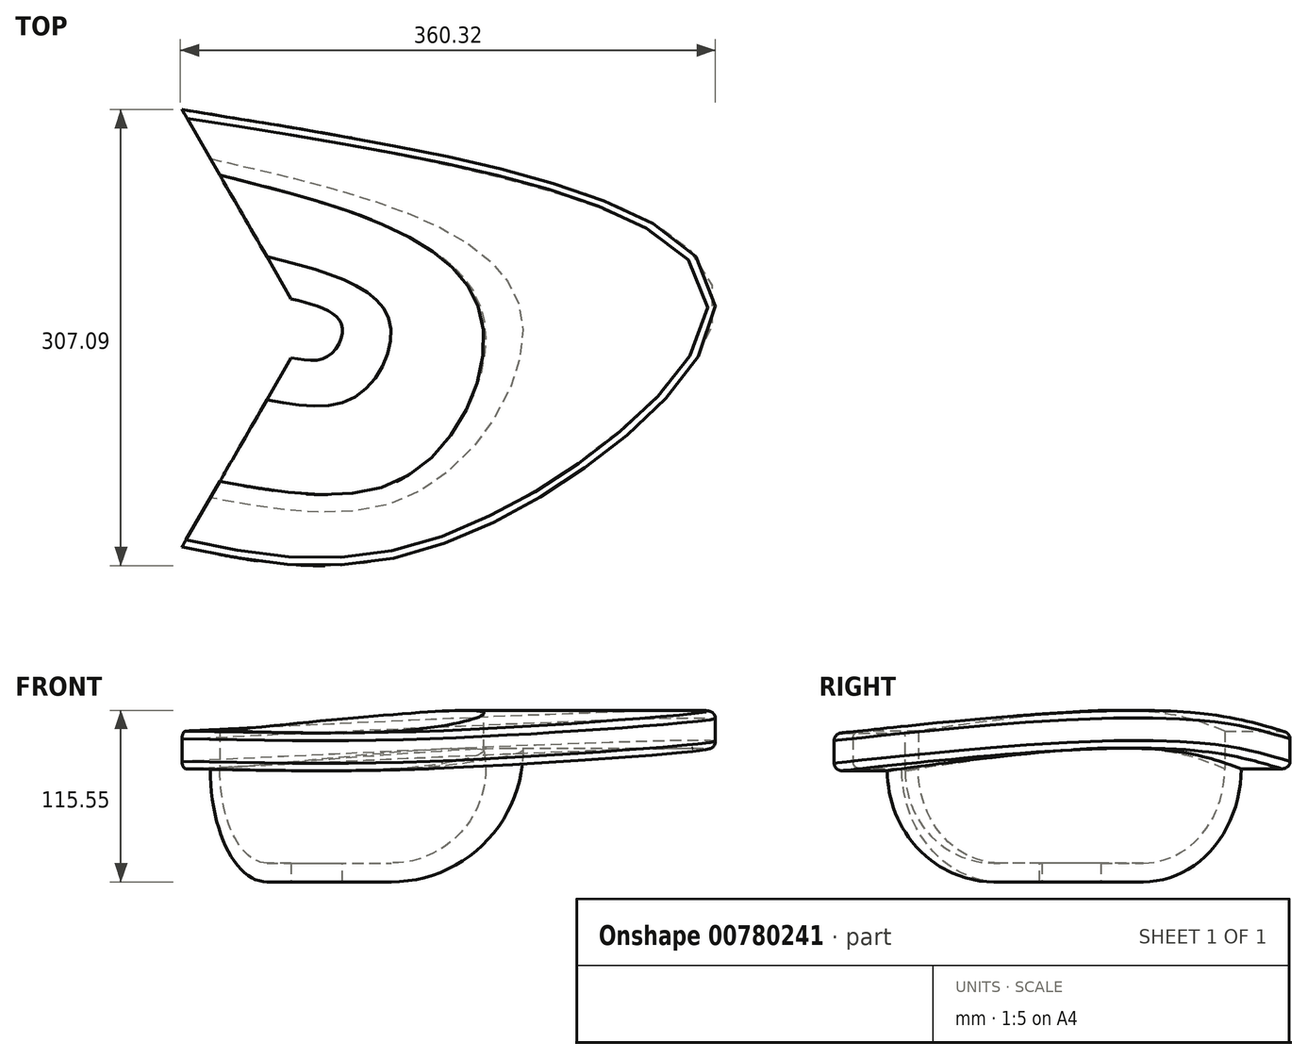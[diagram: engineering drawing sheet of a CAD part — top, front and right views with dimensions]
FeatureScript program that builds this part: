
annotation { "Feature Type Name" : "Feature", "Feature Type Description" : "" }
export const myFeature = defineFeature(function(context is Context, id is Id, definition is map)
    precondition{}
    {
        {
            var Q0;
            Q0=qCreatedBy(makeId("Front.planeOp"),FACE);
            var sketch = newSketch(context, id + "F0", { "sketchPlane" : qUnion([Q0])});
            skLineSegment(sketch, "E0.bottom", {"start": v(-53.34, -12.7) * mm, "end": v(-20.59, -12.7) * mm});
            skLineSegment(sketch, "E0.top", {"start": v(-53.34, -25.4) * mm, "end": v(-20.59, -25.4) * mm});
            skLineSegment(sketch, "E0.left", {"start": v(-53.34, -12.7) * mm, "end": v(-53.34, -25.4) * mm});
            skLineSegment(sketch, "E0.right", {"start": v(-20.59, -12.7) * mm, "end": v(-20.59, -25.4) * mm, "construction": true});
            skLineSegment(sketch, "E1.bottom", {"start": v(41.63, 88.9) * mm, "end": v(195.31, 88.9) * mm});
            skLineSegment(sketch, "E1.top", {"start": v(68.31, 63.5) * mm, "end": v(195.31, 63.5) * mm});
            skLineSegment(sketch, "E1.left", {"start": v(41.63, 88.9) * mm, "end": v(41.63, 63.5) * mm});
            skLineSegment(sketch, "E1.right", {"start": v(195.31, 88.9) * mm, "end": v(195.31, 63.5) * mm});
            skArc(sketch, "E2", {"start": v(-20.59, -25.4) * mm, "mid": v(42.28, 0.64) * mm, "end": v(68.31, 63.5) * mm});
            skArc(sketch, "E3", {"start": v(-20.59, -12.7) * mm, "mid": v(28.6, 10.64) * mm, "end": v(41.63, 63.5) * mm});
            skLineSegment(sketch, "E4", {"start": v(-76.3, -25.4) * mm, "end": v(-76.3, 25.4) * mm, "construction": true});
            skSolve(sketch);
        }
        {
            var Q0;
            Q0=sQuery(id+"F0.wireOp",EDGE,"E4");
            cPlane(context, id + "F1", {"entities" : qUnion([Q0]), "cplaneType" : CPlaneType.LINE_ANGLE, "offset" : 25.4 * mm, "angle" : 30 * degree, "width" : 152.4 * mm, "height" : 152.4 * mm});
        }
        {
            var Q0;
            Q0=qCreatedBy(id+"F1.planeOp",FACE);
            var sketch = newSketch(context, id + "F2", { "sketchPlane" : qUnion([Q0])});
            skLineSegment(sketch, "E5.bottom", {"start": v(61.12, -12.7) * mm, "end": v(93.87, -12.7) * mm});
            skLineSegment(sketch, "E5.top", {"start": v(61.12, -25.4) * mm, "end": v(93.87, -25.4) * mm});
            skLineSegment(sketch, "E5.left", {"start": v(61.12, -12.7) * mm, "end": v(61.12, -25.4) * mm});
            skLineSegment(sketch, "E5.right", {"start": v(93.87, -12.7) * mm, "end": v(93.87, -25.4) * mm, "construction": true});
            skLineSegment(sketch, "E6.bottom", {"start": v(157.37, 76.2) * mm, "end": v(208.17, 76.2) * mm});
            skLineSegment(sketch, "E6.top", {"start": v(170.07, 50.8) * mm, "end": v(208.17, 50.8) * mm});
            skLineSegment(sketch, "E6.left", {"start": v(157.37, 76.2) * mm, "end": v(157.37, 50.8) * mm});
            skLineSegment(sketch, "E6.right", {"start": v(208.17, 76.2) * mm, "end": v(208.17, 50.8) * mm});
            skArc(sketch, "E7", {"start": v(93.87, -25.4) * mm, "mid": v(147.75, -3.08) * mm, "end": v(170.07, 50.8) * mm});
            skArc(sketch, "E8", {"start": v(93.87, -12.7) * mm, "mid": v(138.77, 5.9) * mm, "end": v(157.37, 50.8) * mm});
            skLineSegment(sketch, "E9", {"start": v(38.15, -25.4) * mm, "end": v(38.15, 25.4) * mm, "construction": true});
            skSolve(sketch);
        }
        {
            var Q0;
            Q0=sQuery(id+"F2.wireOp",EDGE,"E9");
            cPlane(context, id + "F3", {"entities" : qUnion([Q0]), "cplaneType" : CPlaneType.LINE_ANGLE, "offset" : 25.4 * mm, "angle" : 150 * degree, "oppositeDirection" : true, "width" : 152.4 * mm, "height" : 152.4 * mm});
        }
        {
            var Q0;
            Q0=qCreatedBy(id+"F3.planeOp",FACE);
            var sketch = newSketch(context, id + "F4", { "sketchPlane" : qUnion([Q0])});
            skLineSegment(sketch, "E10.bottom", {"start": v(-15.18, -12.7) * mm, "end": v(17.56, -12.7) * mm});
            skLineSegment(sketch, "E10.top", {"start": v(-15.18, -25.4) * mm, "end": v(17.56, -25.4) * mm});
            skLineSegment(sketch, "E10.left", {"start": v(-15.18, -12.7) * mm, "end": v(-15.18, -25.4) * mm});
            skLineSegment(sketch, "E10.right", {"start": v(17.56, -12.7) * mm, "end": v(17.56, -25.4) * mm, "construction": true});
            skLineSegment(sketch, "E11.bottom", {"start": v(81.06, 76.2) * mm, "end": v(131.86, 76.2) * mm});
            skLineSegment(sketch, "E11.top", {"start": v(93.76, 50.8) * mm, "end": v(131.86, 50.8) * mm});
            skLineSegment(sketch, "E11.left", {"start": v(81.06, 76.2) * mm, "end": v(81.06, 50.8) * mm});
            skLineSegment(sketch, "E11.right", {"start": v(131.86, 76.2) * mm, "end": v(131.86, 50.8) * mm});
            skArc(sketch, "E12", {"start": v(17.56, -25.4) * mm, "mid": v(71.45, -3.08) * mm, "end": v(93.76, 50.8) * mm});
            skArc(sketch, "E13", {"start": v(17.56, -12.7) * mm, "mid": v(62.47, 5.9) * mm, "end": v(81.06, 50.8) * mm});
            skLineSegment(sketch, "E14", {"start": v(-38.15, -25.4) * mm, "end": v(-38.15, 25.4) * mm, "construction": true});
            skSolve(sketch);
        }
        {
            var Q0;
            Q0=sQuery(id+"F4.wireOp",EDGE,"E14");
            cPlane(context, id + "F5", {"entities" : qUnion([Q0]), "cplaneType" : CPlaneType.LINE_ANGLE, "offset" : 25.4 * mm, "angle" : 150 * degree, "width" : 152.4 * mm, "height" : 152.4 * mm});
        }
        {
            var Q0;
            Q0=qCreatedBy(id+"F5.planeOp",FACE);
            var sketch = newSketch(context, id + "F6", { "sketchPlane" : qUnion([Q0])});
            skLineSegment(sketch, "E15.bottom", {"start": v(61.12, -12.7) * mm, "end": v(93.87, -12.7) * mm});
            skLineSegment(sketch, "E15.top", {"start": v(61.12, -25.4) * mm, "end": v(93.87, -25.4) * mm});
            skLineSegment(sketch, "E15.left", {"start": v(61.12, -12.7) * mm, "end": v(61.12, -25.4) * mm});
            skLineSegment(sketch, "E15.right", {"start": v(93.87, -12.7) * mm, "end": v(93.87, -25.4) * mm, "construction": true});
            skLineSegment(sketch, "E16.bottom", {"start": v(157.37, 76.2) * mm, "end": v(208.17, 76.2) * mm});
            skLineSegment(sketch, "E16.top", {"start": v(170.07, 50.8) * mm, "end": v(208.17, 50.8) * mm});
            skLineSegment(sketch, "E16.left", {"start": v(157.37, 76.2) * mm, "end": v(157.37, 50.8) * mm});
            skLineSegment(sketch, "E16.right", {"start": v(208.17, 76.2) * mm, "end": v(208.17, 50.8) * mm});
            skArc(sketch, "E17", {"start": v(93.87, -25.4) * mm, "mid": v(147.75, -3.08) * mm, "end": v(170.07, 50.8) * mm});
            skArc(sketch, "E18", {"start": v(93.87, -12.7) * mm, "mid": v(138.77, 5.9) * mm, "end": v(157.37, 50.8) * mm});
            skLineSegment(sketch, "E19", {"start": v(38.15, -25.4) * mm, "end": v(38.15, 25.4) * mm, "construction": true});
            skSolve(sketch);
        }
        {
            var Q0;
            Q0 = qSketchRegion(id + "F2", true);
            var Q1;
            Q1 = qSketchRegion(id + "F0", true);
            var Q2;
            Q2 = qSketchRegion(id + "F4", true);
            var Q3;
            Q3 = qSketchRegion(id + "F6", true);
            loft(context, id + "F7", {"sheetProfilesArray" : [{ "sheetProfileEntities" : qUnion([Q0]) }, { "sheetProfileEntities" : qUnion([Q1]) }, { "sheetProfileEntities" : qUnion([Q2]) }, { "sheetProfileEntities" : qUnion([Q3]) }]});
        }
        {
            var Q0;
            Q0=makeQuery(id+"F7.opLoft","SWEPT_EDGE",EDGE,{"disambiguationData":[OSD([sQuery(id+"F0.wireOp",EDGE,"E1.bottom"),sQuery(id+"F0.wireOp",EDGE,"E1.right"),sQuery(id+"F2.wireOp",EDGE,"E6.bottom"),sQuery(id+"F2.wireOp",EDGE,"E6.right")])]});
            var Q1;
            Q1=makeQuery(id+"F7.opLoft","SWEPT_EDGE",EDGE,{"disambiguationData":[OSD([sQuery(id+"F0.wireOp",EDGE,"E1.top"),sQuery(id+"F0.wireOp",EDGE,"E1.right"),sQuery(id+"F2.wireOp",EDGE,"E6.top"),sQuery(id+"F2.wireOp",EDGE,"E6.right")])]});
            fillet(context, id + "F8", {"entities" : qUnion([Q0, Q1]), "radius" : 5.08 * mm, "tangentPropagation" : true, "allowEdgeOverflow" : false});
        }
    });
